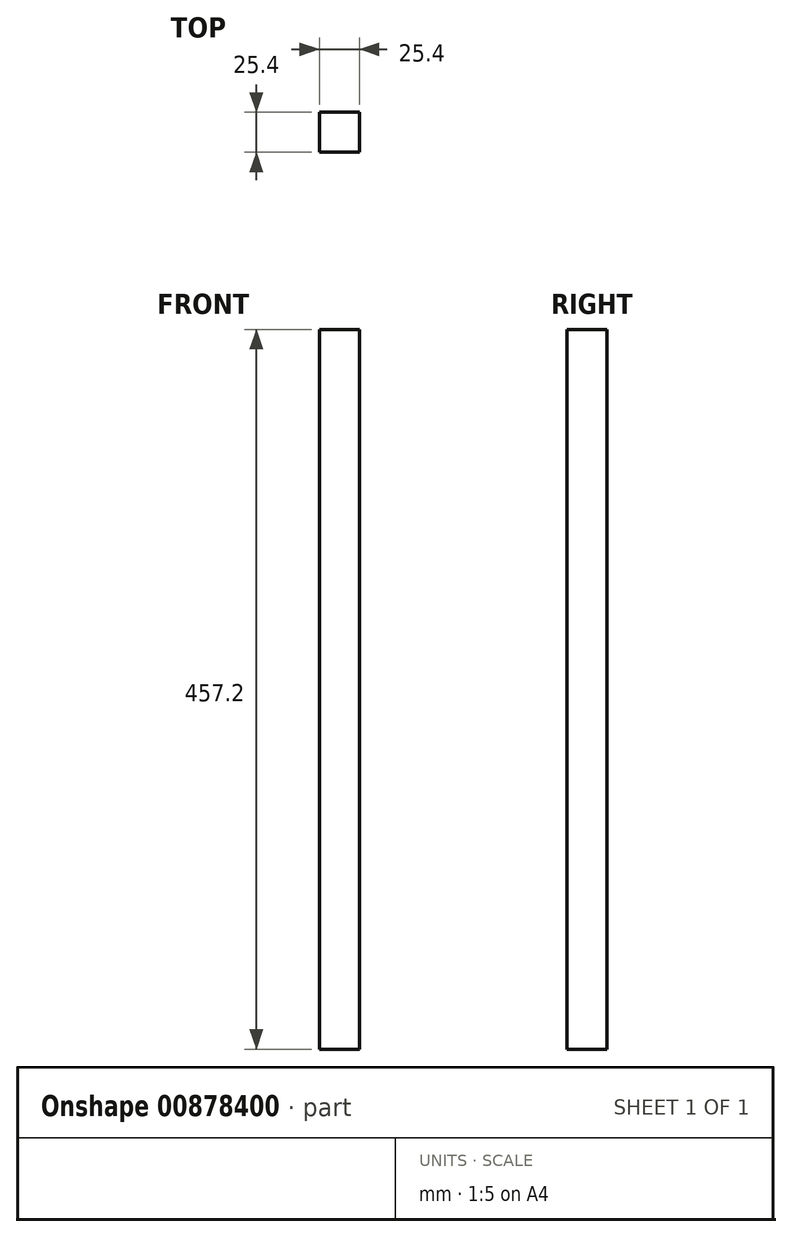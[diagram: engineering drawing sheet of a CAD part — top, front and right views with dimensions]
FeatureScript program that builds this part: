
annotation { "Feature Type Name" : "Feature", "Feature Type Description" : "" }
export const myFeature = defineFeature(function(context is Context, id is Id, definition is map)
    precondition{}
    {
        {
            var Q0;
            Q0=qCreatedBy(makeId("Front.planeOp"),FACE);
            var sketch = newSketch(context, id + "F0", { "sketchPlane" : qUnion([Q0])});
            skLineSegment(sketch, "E0.bottom", {"start": v(0, 0) * mm, "end": v(25.4, 0) * mm});
            skLineSegment(sketch, "E0.top", {"start": v(0, 457.2) * mm, "end": v(25.4, 457.2) * mm});
            skLineSegment(sketch, "E0.left", {"start": v(0, 0) * mm, "end": v(0, 457.2) * mm});
            skLineSegment(sketch, "E0.right", {"start": v(25.4, 0) * mm, "end": v(25.4, 457.2) * mm});
            skSolve(sketch);
        }
        {
            var Q0;
            Q0=makeQuery(id+"F0.imprint","IMPRINT",FACE,{"disambiguationData":[TD([[makeQuery(id+"F0.imprint","IMPRINT",EDGE,{"derivedFrom":sQuery(id+"F0.wireOp",EDGE,"E0.bottom")}),1.0]])]});
            extrude(context, id + "F1", {"entities" : qUnion([Q0]), "depth" : 25.4 * mm, "offsetDistance" : 25.4 * mm});
        }
    });
